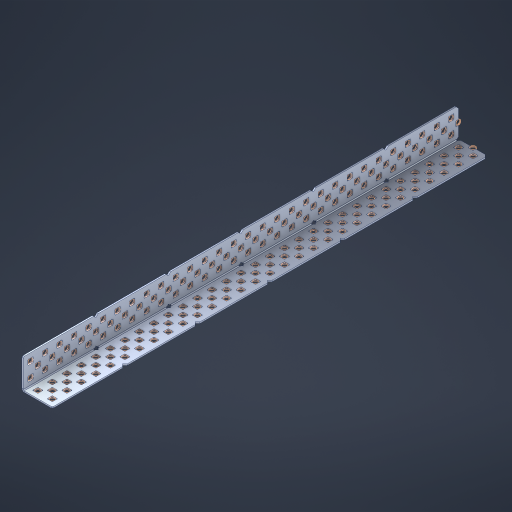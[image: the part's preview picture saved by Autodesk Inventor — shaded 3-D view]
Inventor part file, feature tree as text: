
AUTODESK INVENTOR PART (.ipt)
format: ipt  version: 2023 (Build 270158000, 158)  size: 2,031,104 bytes
history: native  units: in
note: dims shown in document units (in); Inventor stores cm internally (conversion verified against a paired STEP export)
features: other x186, extrude x178, sheet_metal_op x8, sketch x7, pattern_linear x2, mirror x1, chamfer x1
ambient origin geometry x8: Origin, YZ Plane, XZ Plane, XY Plane, X Axis, Y Axis, Z Axis, Center Point
bodies: Solid1 (feature_tree), Body (feature_tree)
feature tree (383):
  sheet_metal_op  "Flanges"
  sheet_metal_op  "Body Pattern"
  pattern_linear  "Center Pattern"  Spacing1=1.0in  [1 undecoded]
  other  "Arc Length"
  pattern_linear  "Notch Pattern"  Spacing1=0.1875in  [1 undecoded]
  other  "Diagonal Plane"
  mirror  "Everything Mirrored"
  chamfer  "End Chamfer"
  sketch  "Sketch1"  dims[d0=1.0in]
  other  "Plate1"
  sketch  "Sketch2"  dims[d1=15.0in]
  other  "Plate2"
  sheet_metal_op  "Bend1"
  sheet_metal_op  "Corner1"
  sketch  "Sketch8"  dims[d2=0.0469in]
  sketch  "Sketch9"  dims[d3=0.0469in]
  other  "Srf91"
  sheet_metal_op  "Body Pattern Sketch"
  other  "Srf92"
  sketch  "Sketch13"  dims[d4=0.0234in]
  sketch  "Sketch15"  dims[d5=0.0938in]
  sketch  "Sketch16"  dims[d6=0.0469in d7=1.0in d8=90.0deg d9=0.0312in d10=0.1875in d11=0.0469in d12=0.0469in d49=0.182in d50=0.02in d52=0.25in d53=0.0469in d54=0.0in d55=0.172in d56=1.0in d57=0.0in d60=11.811in d62=0.5in d63=0.7874in d65=0.5in d85=0.1473in d86=0.1659in d89=0.0469in d90=0.0in d91=0.04in d92=0.0491in d95=2.5in d96=0.04in d97=0.25in d98=45.0deg d99=0.25in d106=0.182in d107=0.02in d108=0.5in d110=0.0469in d111=0.0in d112=0.172in d113=0.5in d114=0.0in d117=0.5in d123=0.25in d125=0.25in d126=0.0491in d127=0.1227in d128=0.08in d129=0.04in d130=2.5in]
  other  "Srf786"
  other  "Srf856"
  other  "Srf857"
  other  "Srf858"
  other  "Srf859"
  other  "Srf860"
  other  "Srf861"
  other  "Srf889"
  other  "Srf890"
  other  "Srf891"
  other  "Srf1275"
  other  "Srf1276"
  other  "Srf1278"
  other  "Srf1279"
  other  "Srf1280"
  other  "Srf1281"
  other  "Srf1282"
  other  "Srf1283"
  other  "Srf1277"
  other  "Srf1285"
  other  "Srf1286"
  other  "Srf1287"
  other  "Srf1383"
  other  "Srf1384"
  other  "Srf1385"
  other  "Srf1386"
  other  "Srf1387"
  other  "Srf1388"
  other  "Srf1389"
  other  "Srf1390"
  other  "Srf1391"
  other  "Srf1392"
  other  "Srf1393"
  other  "Srf1394"
  other  "Srf1395"
  other  "Srf1396"
  other  "Srf1397"
  other  "Srf1398"
  other  "Srf1399"
  other  "Srf1400"
  other  "Srf1401"
  other  "Srf1402"
  other  "Srf1403"
  other  "Srf1404"
  other  "Srf1405"
  other  "Srf1406"
  other  "Srf1407"
  other  "Srf1408"
  other  "Srf1409"
  other  "Srf1410"
  other  "Srf1411"
  other  "Srf1412"
  other  "Srf1413"
  other  "Srf1414"
  other  "Srf1415"
  other  "Srf1416"
  other  "Srf1417"
  other  "Srf1418"
  other  "Srf1419"
  other  "Srf1420"
  other  "Srf1421"
  other  "Srf1422"
  other  "Srf1423"
  other  "Srf1424"
  other  "Srf1425"
  other  "Srf1426"
  other  "Srf1427"
  other  "Srf1428"
  other  "Srf1429"
  other  "Srf1430"
  other  "Srf1431"
  other  "Srf1432"
  other  "Srf1433"
  other  "Srf1434"
  other  "Srf1445"
  other  "Srf1446"
  other  "Srf1447"
  other  "Srf1448"
  other  "Srf1449"
  other  "Srf1450"
  other  "Srf1451"
  other  "Srf1452"
  other  "Srf1453"
  other  "Srf1454"
  other  "Srf1455"
  other  "Srf1456"
  other  "Srf1457"
  other  "Srf1458"
  other  "Srf1459"
  other  "Srf1460"
  other  "Srf1461"
  other  "Srf1462"
  other  "Srf1463"
  other  "Srf1464"
  other  "Srf1465"
  other  "Srf1466"
  other  "Srf1467"
  other  "Srf1468"
  other  "Srf1469"
  other  "Srf1470"
  other  "Srf1475"
  other  "Srf1476"
  other  "Srf1477"
  other  "Srf1478"
  other  "Srf1479"
  other  "Srf1480"
  other  "Srf1481"
  other  "Srf1482"
  other  "Srf1483"
  other  "Srf1484"
  other  "Srf1485"
  other  "Srf1486"
  other  "Srf1487"
  other  "Srf1488"
  other  "Srf1489"
  other  "Srf1490"
  other  "Srf1491"
  other  "Srf1492"
  other  "Srf1493"
  other  "Srf1494"
  other  "Srf1495"
  other  "Srf1496"
  other  "Srf1497"
  other  "Srf1498"
  other  "Srf1499"
  other  "Srf1500"
  other  "Srf1501"
  other  "Srf1502"
  other  "Srf1503"
  other  "Srf1504"
  other  "Srf1505"
  other  "Srf1506"
  other  "Srf1507"
  other  "Srf1508"
  other  "Srf1509"
  other  "Srf1510"
  other  "Srf1511"
  other  "Srf1512"
  other  "Srf1513"
  other  "Srf1514"
  other  "Srf1515"
  other  "Srf1516"
  other  "Srf1517"
  other  "Srf1518"
  other  "Srf1519"
  other  "Srf1520"
  other  "Srf1521"
  other  "Srf1522"
  other  "Srf1523"
  other  "Srf1524"
  other  "Srf1525"
  other  "Srf1526"
  other  "Srf1537"
  other  "Srf1538"
  other  "Srf1539"
  other  "Srf1540"
  other  "Srf1541"
  other  "Srf1542"
  other  "Srf1543"
  other  "Srf1544"
  other  "Srf1545"
  other  "Srf1546"
  other  "Srf1547"
  other  "Srf1548"
  other  "Srf1549"
  other  "Srf1550"
  other  "Srf1551"
  other  "Srf1552"
  other  "Srf1553"
  other  "Srf1554"
  other  "Srf1555"
  other  "Srf1556"
  other  "Srf1557"
  other  "Srf1558"
  other  "Srf1559"
  other  "Srf1560"
  other  "Srf1561"
  other  "Srf1562"
  sheet_metal_op  "Body Stamp"
  sheet_metal_op  "Body Circle"
  other  "Center Stamp"
  other  "Center Circle"
  sheet_metal_op  "Notch"
  extrude  "ExtrusionSrf92"  Depth=0.0469in
  extrude  "ExtrusionSrf856"  Depth=0.0469in
  extrude  "ExtrusionSrf857"  Depth=2.5in
  extrude  "ExtrusionSrf858"  Depth=0.02in
  extrude  "ExtrusionSrf859"  Depth=2.5in
  extrude  "ExtrusionSrf860"  Depth=0.0469in
  extrude  "ExtrusionSrf861"  TaperAngle=0.0deg  [1 undecoded]
  extrude  "ExtrusionSrf889"  Depth=2.5in
  extrude  "ExtrusionSrf890"  Depth=1.0in TaperAngle=0.0deg
  extrude  "ExtrusionSrf891"  Depth=2.5in
  extrude  "ExtrusionSrf1275"  Depth=0.5in
  extrude  "ExtrusionSrf1276"  Depth=2.5in
  extrude  "ExtrusionSrf1277"  Depth=2.5in
  extrude  "ExtrusionSrf1278"  Depth=0.0469in
  extrude  "ExtrusionSrf1279"  Depth=2.5in TaperAngle=0.0deg
  extrude  "ExtrusionSrf1280"  Depth=2.5in
  extrude  "ExtrusionSrf1281"  Depth=2.5in TaperAngle=45.0deg
  extrude  "ExtrusionSrf1282"  Depth=2.5in
  extrude  "ExtrusionSrf1345"  Depth=2.5in
  extrude  "ExtrusionSrf1346"  Depth=0.02in
  extrude  "ExtrusionSrf1347"  Depth=0.5in
  extrude  "ExtrusionSrf1348"  Depth=0.0469in
  extrude  "ExtrusionSrf1383"  TaperAngle=0.0deg  [1 undecoded]
  extrude  "ExtrusionSrf1384"  Depth=2.5in
  extrude  "ExtrusionSrf1385"  Depth=0.5in TaperAngle=0.0deg
  extrude  "ExtrusionSrf1386"  Depth=0.5in
  extrude  "ExtrusionSrf1387"  Depth=2.5in
  extrude  "ExtrusionSrf1388"  Depth=2.5in
  extrude  "ExtrusionSrf1389"  Depth=2.5in
  extrude  "ExtrusionSrf1390"  Depth=2.5in
  extrude  "ExtrusionSrf1391"  Depth=2.5in
  extrude  "ExtrusionSrf1392"  Depth=2.5in
  extrude  "ExtrusionSrf1393"  Depth=2.5in
  extrude  "ExtrusionSrf1394"  [1 undecoded]
  extrude  "ExtrusionSrf1395"  [1 undecoded]
  extrude  "ExtrusionSrf1396"  [1 undecoded]
  extrude  "ExtrusionSrf1397"  [1 undecoded]
  extrude  "ExtrusionSrf1398"  [1 undecoded]
  extrude  "ExtrusionSrf1399"  [1 undecoded]
  extrude  "ExtrusionSrf1400"  [1 undecoded]
  extrude  "ExtrusionSrf1401"  [1 undecoded]
  extrude  "ExtrusionSrf1402"  [1 undecoded]
  extrude  "ExtrusionSrf1403"  [1 undecoded]
  extrude  "ExtrusionSrf1404"  [1 undecoded]
  extrude  "ExtrusionSrf1405"  [1 undecoded]
  extrude  "ExtrusionSrf1406"  [1 undecoded]
  extrude  "ExtrusionSrf1407"  [1 undecoded]
  extrude  "ExtrusionSrf1408"  [1 undecoded]
  extrude  "ExtrusionSrf1409"  [1 undecoded]
  extrude  "ExtrusionSrf1410"  [1 undecoded]
  extrude  "ExtrusionSrf1411"  [1 undecoded]
  extrude  "ExtrusionSrf1412"  [1 undecoded]
  extrude  "ExtrusionSrf1413"  [1 undecoded]
  extrude  "ExtrusionSrf1414"  [1 undecoded]
  extrude  "ExtrusionSrf1415"  [1 undecoded]
  extrude  "ExtrusionSrf1416"  [1 undecoded]
  extrude  "ExtrusionSrf1417"  [1 undecoded]
  extrude  "ExtrusionSrf1418"  [1 undecoded]
  extrude  "ExtrusionSrf1419"  [1 undecoded]
  extrude  "ExtrusionSrf1420"  [1 undecoded]
  extrude  "ExtrusionSrf1421"  [1 undecoded]
  extrude  "ExtrusionSrf1422"  [1 undecoded]
  extrude  "ExtrusionSrf1423"  [1 undecoded]
  extrude  "ExtrusionSrf1424"  [1 undecoded]
  extrude  "ExtrusionSrf1425"  [1 undecoded]
  extrude  "ExtrusionSrf1426"  [1 undecoded]
  extrude  "ExtrusionSrf1427"  [1 undecoded]
  extrude  "ExtrusionSrf1428"  [1 undecoded]
  extrude  "ExtrusionSrf1429"  [1 undecoded]
  extrude  "ExtrusionSrf1430"  [1 undecoded]
  extrude  "ExtrusionSrf1431"  [1 undecoded]
  extrude  "ExtrusionSrf1432"  [1 undecoded]
  extrude  "ExtrusionSrf1433"  [1 undecoded]
  extrude  "ExtrusionSrf1434"  [1 undecoded]
  extrude  "ExtrusionSrf1445"  [1 undecoded]
  extrude  "ExtrusionSrf1446"  [1 undecoded]
  extrude  "ExtrusionSrf1447"  [1 undecoded]
  extrude  "ExtrusionSrf1448"  [1 undecoded]
  extrude  "ExtrusionSrf1449"  [1 undecoded]
  extrude  "ExtrusionSrf1450"  [1 undecoded]
  extrude  "ExtrusionSrf1451"  [1 undecoded]
  extrude  "ExtrusionSrf1452"  [1 undecoded]
  extrude  "ExtrusionSrf1453"  [1 undecoded]
  extrude  "ExtrusionSrf1454"  [1 undecoded]
  extrude  "ExtrusionSrf1455"  [1 undecoded]
  extrude  "ExtrusionSrf1456"  [1 undecoded]
  extrude  "ExtrusionSrf1457"  [1 undecoded]
  extrude  "ExtrusionSrf1458"  [1 undecoded]
  extrude  "ExtrusionSrf1459"  [1 undecoded]
  extrude  "ExtrusionSrf1460"  [1 undecoded]
  extrude  "ExtrusionSrf1461"  [1 undecoded]
  extrude  "ExtrusionSrf1462"  [1 undecoded]
  extrude  "ExtrusionSrf1463"  [1 undecoded]
  extrude  "ExtrusionSrf1464"  [1 undecoded]
  extrude  "ExtrusionSrf1465"  [1 undecoded]
  extrude  "ExtrusionSrf1466"  [1 undecoded]
  extrude  "ExtrusionSrf1467"  [1 undecoded]
  extrude  "ExtrusionSrf1468"  [1 undecoded]
  extrude  "ExtrusionSrf1469"  [1 undecoded]
  extrude  "ExtrusionSrf1470"  [1 undecoded]
  extrude  "ExtrusionSrf1475"  [1 undecoded]
  extrude  "ExtrusionSrf1476"  [1 undecoded]
  extrude  "ExtrusionSrf1477"  [1 undecoded]
  extrude  "ExtrusionSrf1478"  [1 undecoded]
  extrude  "ExtrusionSrf1479"  [1 undecoded]
  extrude  "ExtrusionSrf1480"  [1 undecoded]
  extrude  "ExtrusionSrf1481"  [1 undecoded]
  extrude  "ExtrusionSrf1482"  [1 undecoded]
  extrude  "ExtrusionSrf1483"  [1 undecoded]
  extrude  "ExtrusionSrf1484"  [1 undecoded]
  extrude  "ExtrusionSrf1485"  [1 undecoded]
  extrude  "ExtrusionSrf1486"  [1 undecoded]
  extrude  "ExtrusionSrf1487"  [1 undecoded]
  extrude  "ExtrusionSrf1488"  [1 undecoded]
  extrude  "ExtrusionSrf1489"  [1 undecoded]
  extrude  "ExtrusionSrf1490"  [1 undecoded]
  extrude  "ExtrusionSrf1491"  [1 undecoded]
  extrude  "ExtrusionSrf1492"  [1 undecoded]
  extrude  "ExtrusionSrf1493"  [1 undecoded]
  extrude  "ExtrusionSrf1494"  [1 undecoded]
  extrude  "ExtrusionSrf1495"  [1 undecoded]
  extrude  "ExtrusionSrf1496"  [1 undecoded]
  extrude  "ExtrusionSrf1497"  [1 undecoded]
  extrude  "ExtrusionSrf1498"  [1 undecoded]
  extrude  "ExtrusionSrf1499"  [1 undecoded]
  extrude  "ExtrusionSrf1500"  [1 undecoded]
  extrude  "ExtrusionSrf1501"  [1 undecoded]
  extrude  "ExtrusionSrf1502"  [1 undecoded]
  extrude  "ExtrusionSrf1503"  [1 undecoded]
  extrude  "ExtrusionSrf1504"  [1 undecoded]
  extrude  "ExtrusionSrf1505"  [1 undecoded]
  extrude  "ExtrusionSrf1506"  [1 undecoded]
  extrude  "ExtrusionSrf1507"  [1 undecoded]
  extrude  "ExtrusionSrf1508"  [1 undecoded]
  extrude  "ExtrusionSrf1509"  [1 undecoded]
  extrude  "ExtrusionSrf1510"  [1 undecoded]
  extrude  "ExtrusionSrf1511"  [1 undecoded]
  extrude  "ExtrusionSrf1512"  [1 undecoded]
  extrude  "ExtrusionSrf1513"  [1 undecoded]
  extrude  "ExtrusionSrf1514"  [1 undecoded]
  extrude  "ExtrusionSrf1515"  [1 undecoded]
  extrude  "ExtrusionSrf1516"  [1 undecoded]
  extrude  "ExtrusionSrf1517"  [1 undecoded]
  extrude  "ExtrusionSrf1518"  [1 undecoded]
  extrude  "ExtrusionSrf1519"  [1 undecoded]
  extrude  "ExtrusionSrf1520"  [1 undecoded]
  extrude  "ExtrusionSrf1521"  [1 undecoded]
  extrude  "ExtrusionSrf1522"  [1 undecoded]
  extrude  "ExtrusionSrf1523"  [1 undecoded]
  extrude  "ExtrusionSrf1524"  [1 undecoded]
  extrude  "ExtrusionSrf1525"  [1 undecoded]
  extrude  "ExtrusionSrf1526"  [1 undecoded]
  extrude  "ExtrusionSrf1537"  [1 undecoded]
  extrude  "ExtrusionSrf1538"  [1 undecoded]
  extrude  "ExtrusionSrf1539"  [1 undecoded]
  extrude  "ExtrusionSrf1540"  [1 undecoded]
  extrude  "ExtrusionSrf1541"  [1 undecoded]
  extrude  "ExtrusionSrf1542"  [1 undecoded]
  extrude  "ExtrusionSrf1543"  [1 undecoded]
  extrude  "ExtrusionSrf1544"  [1 undecoded]
  extrude  "ExtrusionSrf1545"  [1 undecoded]
  extrude  "ExtrusionSrf1546"  [1 undecoded]
  extrude  "ExtrusionSrf1547"  [1 undecoded]
  extrude  "ExtrusionSrf1548"  [1 undecoded]
  extrude  "ExtrusionSrf1549"  [1 undecoded]
  extrude  "ExtrusionSrf1550"  [1 undecoded]
  extrude  "ExtrusionSrf1551"  [1 undecoded]
  extrude  "ExtrusionSrf1552"  [1 undecoded]
  extrude  "ExtrusionSrf1553"  [1 undecoded]
  extrude  "ExtrusionSrf1554"  [1 undecoded]
  extrude  "ExtrusionSrf1555"  [1 undecoded]
  extrude  "ExtrusionSrf1556"  [1 undecoded]
  extrude  "ExtrusionSrf1557"  [1 undecoded]
  extrude  "ExtrusionSrf1558"  [1 undecoded]
  extrude  "ExtrusionSrf1559"  [1 undecoded]
  extrude  "ExtrusionSrf1560"  [1 undecoded]
  extrude  "ExtrusionSrf1561"  [1 undecoded]
  extrude  "ExtrusionSrf1562"  [1 undecoded]
note: 149 required parameter values undecoded (feature->parameter linkage not recoverable at this tier; creation-order binding heuristic only, values carry confidence <= 0.55)
